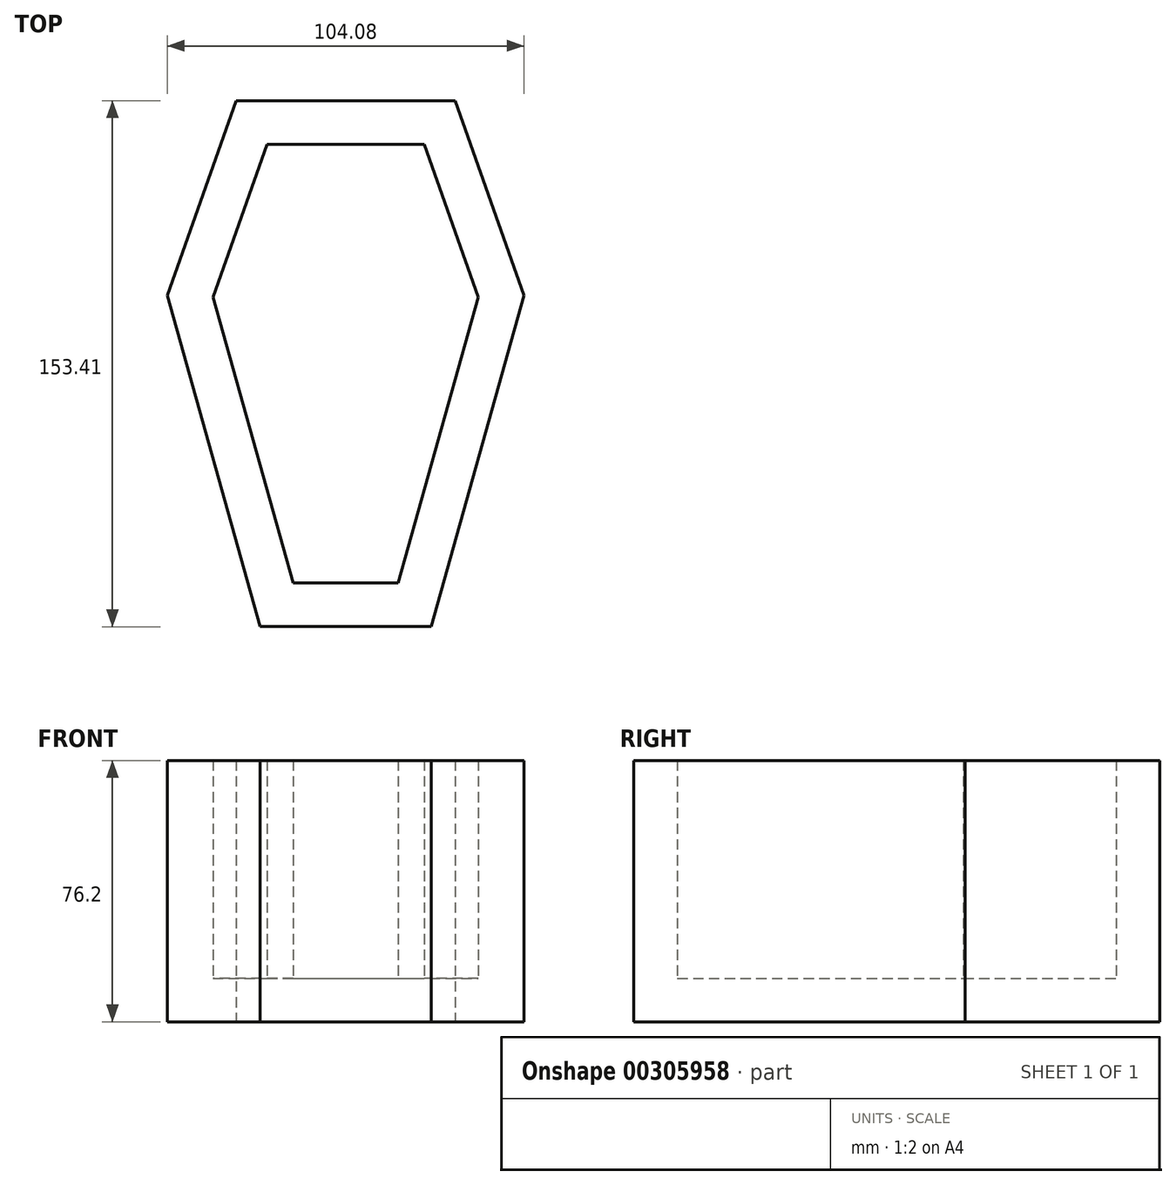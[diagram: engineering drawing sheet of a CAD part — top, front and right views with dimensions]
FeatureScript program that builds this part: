
annotation { "Feature Type Name" : "Feature", "Feature Type Description" : "" }
export const myFeature = defineFeature(function(context is Context, id is Id, definition is map)
    precondition{}
    {
        {
            var Q0;
            Q0=qCreatedBy(makeId("Top.planeOp"),FACE);
            var sketch = newSketch(context, id + "F0", { "sketchPlane" : qUnion([Q0])});
            skLineSegment(sketch, "E0", {"start": v(-24.97, -55.35) * mm, "end": v(-52.04, 41.2) * mm});
            skLineSegment(sketch, "E1", {"start": v(-52.04, 41.2) * mm, "end": v(-31.88, 98.06) * mm});
            skLineSegment(sketch, "E2", {"start": v(-31.88, 98.06) * mm, "end": v(0, 98.06) * mm});
            skLineSegment(sketch, "E3.MirrorCS", {"start": v(52.04, 41.2) * mm, "end": v(31.88, 98.06) * mm});
            skLineSegment(sketch, "E4.MirrorCS", {"start": v(24.97, -55.35) * mm, "end": v(52.04, 41.2) * mm});
            skLineSegment(sketch, "E5", {"start": v(0, 98.06) * mm, "end": v(31.88, 98.06) * mm});
            skLineSegment(sketch, "E6", {"start": v(-24.97, -55.35) * mm, "end": v(24.97, -55.35) * mm});
            skSolve(sketch);
        }
        {
            var Q0;
            Q0 = qSketchRegion(id + "F0", true);
            extrude(context, id + "F1", {"entities" : qUnion([Q0]), "depth" : 76.2 * mm});
        }
        {
            var Q0;
            Q0=makeQuery(id+"F1.opExtrude","CAP_FACE",FACE,{"disambiguationData":[OSD([sQuery(id+"F0.wireOp",EDGE,"E0"),sQuery(id+"F0.wireOp",EDGE,"E1"),sQuery(id+"F0.wireOp",EDGE,"E2"),sQuery(id+"F0.wireOp",EDGE,"E3.MirrorCS"),sQuery(id+"F0.wireOp",EDGE,"E4.MirrorCS"),sQuery(id+"F0.wireOp",EDGE,"E5"),sQuery(id+"F0.wireOp",EDGE,"E6")])],"isStart":false});
            var Q1;
            Q1=makeQuery(id+"F1.opExtrude","SWEPT_BODY",BODY,{"disambiguationData":[OSD([sQuery(id+"F0.wireOp",EDGE,"E0"),sQuery(id+"F0.wireOp",EDGE,"E1"),sQuery(id+"F0.wireOp",EDGE,"E2"),sQuery(id+"F0.wireOp",EDGE,"E3.MirrorCS"),sQuery(id+"F0.wireOp",EDGE,"E4.MirrorCS"),sQuery(id+"F0.wireOp",EDGE,"E5"),sQuery(id+"F0.wireOp",EDGE,"E6")])]});
            shell(context, id + "F2", {"entities" : qUnion([Q0]), "parts" : qUnion([Q1]), "thickness" : 12.7 * mm});
        }
    });
